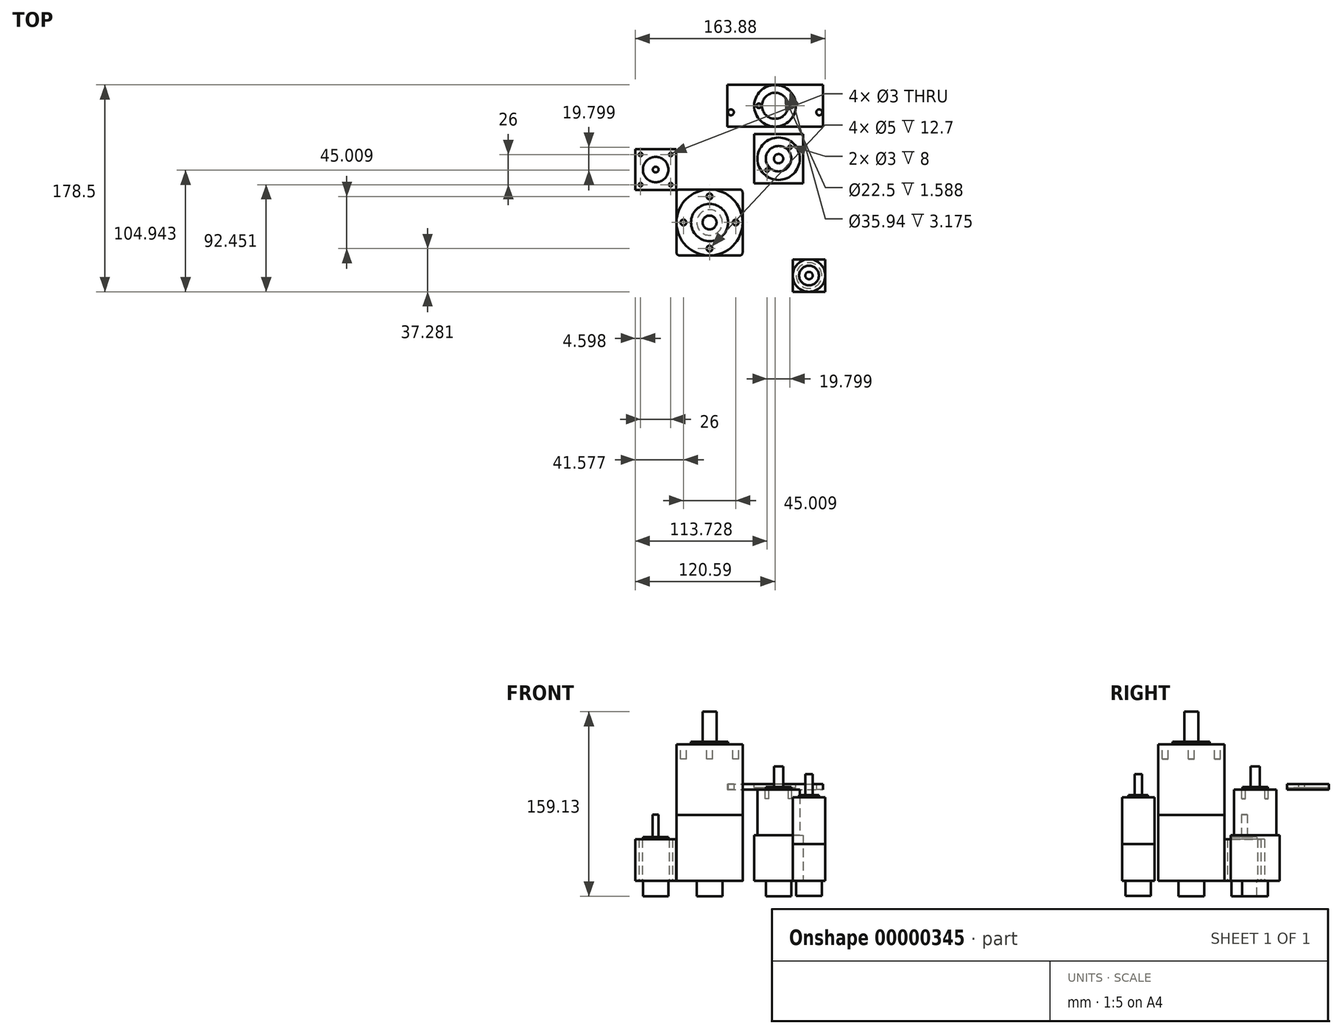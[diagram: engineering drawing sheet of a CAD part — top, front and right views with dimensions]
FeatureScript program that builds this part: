
annotation { "Feature Type Name" : "Feature", "Feature Type Description" : "" }
export const myFeature = defineFeature(function(context is Context, id is Id, definition is map)
    precondition{}
    {
        {
            var Q0;
            Q0=qCreatedBy(makeId("Top.planeOp"),FACE);
            var sketch = newSketch(context, id + "F0", { "sketchPlane" : qUnion([Q0])});
            skLineSegment(sketch, "E0.bottom", {"start": v(-20.35, 13.53) * mm, "end": v(31.57, 13.53) * mm});
            skLineSegment(sketch, "E0.top", {"start": v(-20.35, -43.46) * mm, "end": v(31.57, -43.46) * mm});
            skLineSegment(sketch, "E0.left", {"start": v(-22.89, 11) * mm, "end": v(-22.89, -40.92) * mm});
            skLineSegment(sketch, "E0.right", {"start": v(34.11, 11) * mm, "end": v(34.11, -40.92) * mm});
            skLineSegment(sketch, "E1", {"start": v(-22.89, 13.53) * mm, "end": v(34.11, -43.46) * mm, "construction": true});
            skLineSegment(sketch, "E2", {"start": v(34.11, 13.53) * mm, "end": v(-22.89, -43.46) * mm, "construction": true});
            skCircle(sketch, "E3", {"center": v(5.61, -14.96) * mm, "radius": 28.5 * mm, "construction": true});
            skPoint(sketch, "E4.visualSharp", {"position": v(-22.89, 13.53) * mm});
            skArc(sketch, "E4.filletArc", {"start": v(-20.35, 13.53) * mm, "mid": v(-22.14, 12.8) * mm, "end": v(-22.89, 11) * mm});
            skPoint(sketch, "E5.visualSharp", {"position": v(34.11, 13.53) * mm});
            skArc(sketch, "E5.filletArc", {"start": v(34.11, 11) * mm, "mid": v(33.37, 12.8) * mm, "end": v(31.57, 13.53) * mm});
            skPoint(sketch, "E6.visualSharp", {"position": v(34.11, -43.46) * mm});
            skArc(sketch, "E6.filletArc", {"start": v(31.57, -43.46) * mm, "mid": v(33.37, -42.72) * mm, "end": v(34.11, -40.92) * mm});
            skPoint(sketch, "E7.visualSharp", {"position": v(-22.89, -43.46) * mm});
            skArc(sketch, "E7.filletArc", {"start": v(-22.89, -40.92) * mm, "mid": v(-22.14, -42.72) * mm, "end": v(-20.35, -43.46) * mm});
            skSolve(sketch);
        }
        {
            var Q0;
            Q0=makeQuery(id+"F0.imprint","IMPRINT",FACE,{"disambiguationData":[TD([[makeQuery(id+"F0.imprint","IMPRINT",EDGE,{"derivedFrom":sQuery(id+"F0.wireOp",EDGE,"E0.bottom")}),-1.0]])]});
            extrude(context, id + "F1", {"entities" : qUnion([Q0]), "depth" : 57.02 * mm});
        }
        {
            var Q0;
            Q0=makeQuery(id+"F1.opExtrude","CAP_FACE",FACE,{"disambiguationData":[OSD([sQuery(id+"F0.wireOp",EDGE,"E0.bottom"),sQuery(id+"F0.wireOp",EDGE,"E0.top"),sQuery(id+"F0.wireOp",EDGE,"E0.left"),sQuery(id+"F0.wireOp",EDGE,"E0.right"),sQuery(id+"F0.wireOp",EDGE,"E4.filletArc"),sQuery(id+"F0.wireOp",EDGE,"E5.filletArc"),sQuery(id+"F0.wireOp",EDGE,"E6.filletArc"),sQuery(id+"F0.wireOp",EDGE,"E7.filletArc")])],"isStart":false});
            var sketch = newSketch(context, id + "F2", { "sketchPlane" : qUnion([Q0])});
            skCircle(sketch, "E8", {"center": v(5.61, -14.96) * mm, "radius": 28.5 * mm});
            skSolve(sketch);
        }
        {
            var Q0;
            {var subQ0=sQuery(id+"F2.wireOp",EDGE,"E8");var subQ4=makeQuery(id+"F2.imprint","INTERSECT",VERTEX,{"derivedFrom":[makeQuery(id+"F1.opExtrude","CAP_EDGE",EDGE,{"disambiguationData":[OSD([sQuery(id+"F0.wireOp",EDGE,"E0.bottom")])],"isStart":false}),subQ0]});Q0=makeQuery(id+"F2.imprint","IMPRINT",FACE,{"disambiguationData":[TD([[makeQuery(id+"F2.imprint","IMPRINT",EDGE,{"disambiguationData":[TD([[subQ4,1.0]])],"derivedFrom":subQ0}),1.0]])]});}
            extrude(context, id + "F3", {"entities" : qUnion([Q0]), "operationType" : NewBodyOperationType.ADD, "depth" : 61 * mm});
        }
        {
            var Q0;
            Q0=makeQuery(id+"F3.opExtrude","CAP_FACE",FACE,{"disambiguationData":[OSD([sQuery(id+"F2.wireOp",EDGE,"E8")])],"isStart":false});
            var sketch = newSketch(context, id + "F4", { "sketchPlane" : qUnion([Q0])});
            skCircle(sketch, "E9", {"center": v(5.61, -14.96) * mm, "radius": 16 * mm});
            skSolve(sketch);
        }
        {
            var Q0;
            Q0=makeQuery(id+"F4.imprint","IMPRINT",FACE,{"disambiguationData":[TD([[makeQuery(id+"F4.imprint","IMPRINT",EDGE,{"derivedFrom":sQuery(id+"F4.wireOp",EDGE,"E9")}),1.0]])]});
            extrude(context, id + "F5", {"entities" : qUnion([Q0]), "operationType" : NewBodyOperationType.ADD, "depth" : 2 * mm});
        }
        {
            var Q0;
            Q0=makeQuery(id+"F5.opExtrude","CAP_FACE",FACE,{"disambiguationData":[OSD([sQuery(id+"F4.wireOp",EDGE,"E9")])],"isStart":false});
            var sketch = newSketch(context, id + "F6", { "sketchPlane" : qUnion([Q0])});
            skCircle(sketch, "E10", {"center": v(5.61, -14.96) * mm, "radius": 6 * mm});
            skSolve(sketch);
        }
        {
            var Q0;
            Q0=makeQuery(id+"F6.imprint","IMPRINT",FACE,{"disambiguationData":[TD([[makeQuery(id+"F6.imprint","IMPRINT",EDGE,{"derivedFrom":sQuery(id+"F6.wireOp",EDGE,"E10")}),1.0]])]});
            extrude(context, id + "F7", {"entities" : qUnion([Q0]), "operationType" : NewBodyOperationType.ADD, "depth" : 26 * mm});
        }
        {
            var Q0;
            Q0=makeQuery(id+"F3.opExtrude","CAP_FACE",FACE,{"disambiguationData":[OSD([sQuery(id+"F2.wireOp",EDGE,"E8")])],"isStart":false});
            var sketch = newSketch(context, id + "F8", { "sketchPlane" : qUnion([Q0])});
            skCircle(sketch, "E11", {"center": v(5.61, -14.96) * mm, "radius": 22.5 * mm, "construction": true});
            skCircle(sketch, "E12", {"center": v(5.61, 7.54) * mm, "radius": 2.5 * mm});
            skCircle(sketch, "E13", {"center": v(28.12, -14.96) * mm, "radius": 2.5 * mm});
            skCircle(sketch, "E14", {"center": v(5.61, -37.47) * mm, "radius": 2.5 * mm});
            skCircle(sketch, "E15", {"center": v(-16.9, -14.96) * mm, "radius": 2.5 * mm});
            skSolve(sketch);
        }
        {
            var Q0;
            {Q0=qUnion([makeQuery(id+"F8.imprint","IMPRINT",FACE,{"disambiguationData":[TD([[makeQuery(id+"F8.imprint","IMPRINT",EDGE,{"derivedFrom":sQuery(id+"F8.wireOp",EDGE,"E12")}),1.0]])]}),makeQuery(id+"F8.imprint","IMPRINT",FACE,{"disambiguationData":[TD([[makeQuery(id+"F8.imprint","IMPRINT",EDGE,{"derivedFrom":sQuery(id+"F8.wireOp",EDGE,"E13")}),1.0]])]}),makeQuery(id+"F8.imprint","IMPRINT",FACE,{"disambiguationData":[TD([[makeQuery(id+"F8.imprint","IMPRINT",EDGE,{"derivedFrom":sQuery(id+"F8.wireOp",EDGE,"E14")}),1.0]])]}),makeQuery(id+"F8.imprint","IMPRINT",FACE,{"disambiguationData":[TD([[makeQuery(id+"F8.imprint","IMPRINT",EDGE,{"derivedFrom":sQuery(id+"F8.wireOp",EDGE,"E15")}),1.0]])]})]);}
            extrude(context, id + "F9", {"entities" : qUnion([Q0]), "operationType" : NewBodyOperationType.REMOVE, "oppositeDirection" : true, "depth" : 12.7 * mm});
        }
        {
            var Q0;
            Q0=qCreatedBy(makeId("Top.planeOp"),FACE);
            var sketch = newSketch(context, id + "F10", { "sketchPlane" : qUnion([Q0])});
            skLineSegment(sketch, "E16.bottom", {"start": v(44.01, 61.24) * mm, "end": v(86.3, 61.24) * mm});
            skLineSegment(sketch, "E16.top", {"start": v(44.01, 18.95) * mm, "end": v(86.3, 18.95) * mm});
            skLineSegment(sketch, "E16.left", {"start": v(44.01, 61.24) * mm, "end": v(44.01, 18.95) * mm});
            skLineSegment(sketch, "E16.right", {"start": v(86.3, 61.24) * mm, "end": v(86.3, 18.95) * mm});
            skSolve(sketch);
        }
        {
            var Q0;
            Q0=makeQuery(id+"F10.imprint","IMPRINT",FACE,{"disambiguationData":[TD([[makeQuery(id+"F10.imprint","IMPRINT",EDGE,{"derivedFrom":sQuery(id+"F10.wireOp",EDGE,"E16.bottom")}),-1.0]])]});
            extrude(context, id + "F11", {"entities" : qUnion([Q0]), "depth" : 39.5 * mm});
        }
        {
            var Q0;
            Q0=makeQuery(id+"F11.opExtrude","CAP_FACE",FACE,{"disambiguationData":[OSD([sQuery(id+"F10.wireOp",EDGE,"E16.bottom"),sQuery(id+"F10.wireOp",EDGE,"E16.top"),sQuery(id+"F10.wireOp",EDGE,"E16.left"),sQuery(id+"F10.wireOp",EDGE,"E16.right")])],"isStart":false});
            var sketch = newSketch(context, id + "F12", { "sketchPlane" : qUnion([Q0])});
            skCircle(sketch, "E17", {"center": v(65.16, 40.1) * mm, "radius": 21.15 * mm, "construction": true});
            skCircle(sketch, "E18", {"center": v(65.16, 40.1) * mm, "radius": 18.29 * mm});
            skSolve(sketch);
        }
        {
            var Q0;
            Q0=makeQuery(id+"F12.imprint","IMPRINT",FACE,{"disambiguationData":[TD([[makeQuery(id+"F12.imprint","IMPRINT",EDGE,{"derivedFrom":sQuery(id+"F12.wireOp",EDGE,"E18")}),1.0]])]});
            extrude(context, id + "F13", {"entities" : qUnion([Q0]), "operationType" : NewBodyOperationType.ADD, "depth" : 39.5 * mm});
        }
        {
            var Q0;
            Q0=makeQuery(id+"F13.opExtrude","CAP_FACE",FACE,{"disambiguationData":[OSD([sQuery(id+"F12.wireOp",EDGE,"E18")])],"isStart":false});
            var sketch = newSketch(context, id + "F14", { "sketchPlane" : qUnion([Q0])});
            skCircle(sketch, "E19", {"center": v(65.16, 40.1) * mm, "radius": 11 * mm});
            skSolve(sketch);
        }
        {
            var Q0;
            Q0=makeQuery(id+"F14.imprint","IMPRINT",FACE,{"disambiguationData":[TD([[makeQuery(id+"F14.imprint","IMPRINT",EDGE,{"derivedFrom":sQuery(id+"F14.wireOp",EDGE,"E19")}),1.0]])]});
            extrude(context, id + "F15", {"entities" : qUnion([Q0]), "operationType" : NewBodyOperationType.ADD, "depth" : 1.98 * mm});
        }
        {
            var Q0;
            Q0=makeQuery(id+"F15.opExtrude","CAP_FACE",FACE,{"disambiguationData":[OSD([sQuery(id+"F14.wireOp",EDGE,"E19")])],"isStart":false});
            var sketch = newSketch(context, id + "F16", { "sketchPlane" : qUnion([Q0])});
            skCircle(sketch, "E20", {"center": v(65.16, 40.1) * mm, "radius": 4 * mm});
            skSolve(sketch);
        }
        {
            var Q0;
            Q0=makeQuery(id+"F16.imprint","IMPRINT",FACE,{"disambiguationData":[TD([[makeQuery(id+"F16.imprint","IMPRINT",EDGE,{"derivedFrom":sQuery(id+"F16.wireOp",EDGE,"E20")}),1.0]])]});
            extrude(context, id + "F17", {"entities" : qUnion([Q0]), "operationType" : NewBodyOperationType.ADD, "depth" : 18 * mm});
        }
        {
            var Q0;
            Q0=qCreatedBy(makeId("Top.planeOp"),FACE);
            var sketch = newSketch(context, id + "F18", { "sketchPlane" : qUnion([Q0])});
            skLineSegment(sketch, "E21.bottom", {"start": v(77.42, -46.76) * mm, "end": v(105.4, -46.76) * mm});
            skLineSegment(sketch, "E21.top", {"start": v(77.42, -74.75) * mm, "end": v(105.4, -74.75) * mm});
            skLineSegment(sketch, "E21.left", {"start": v(77.42, -46.76) * mm, "end": v(77.42, -74.75) * mm});
            skLineSegment(sketch, "E21.right", {"start": v(105.4, -46.76) * mm, "end": v(105.4, -74.75) * mm});
            skSolve(sketch);
        }
        {
            var Q0;
            Q0=makeQuery(id+"F18.imprint","IMPRINT",FACE,{"disambiguationData":[TD([[makeQuery(id+"F18.imprint","IMPRINT",EDGE,{"derivedFrom":sQuery(id+"F18.wireOp",EDGE,"E21.bottom")}),-1.0]])]});
            extrude(context, id + "F19", {"entities" : qUnion([Q0]), "depth" : 32 * mm});
        }
        {
            var Q0;
            Q0=makeQuery(id+"F19.opExtrude","CAP_FACE",FACE,{"disambiguationData":[OSD([sQuery(id+"F18.wireOp",EDGE,"E21.bottom"),sQuery(id+"F18.wireOp",EDGE,"E21.top"),sQuery(id+"F18.wireOp",EDGE,"E21.left"),sQuery(id+"F18.wireOp",EDGE,"E21.right")])],"isStart":false});
            var sketch = newSketch(context, id + "F20", { "sketchPlane" : qUnion([Q0])});
            skLineSegment(sketch, "E22.0.0", {"start": v(77.42, -46.76) * mm, "end": v(105.4, -46.76) * mm, "construction": true});
            skLineSegment(sketch, "E22.0.1", {"start": v(77.42, -46.76) * mm, "end": v(77.42, -74.75) * mm, "construction": true});
            skLineSegment(sketch, "E22.0.2", {"start": v(77.42, -74.75) * mm, "end": v(105.4, -74.75) * mm, "construction": true});
            skLineSegment(sketch, "E22.0.3", {"start": v(105.4, -46.76) * mm, "end": v(105.4, -74.75) * mm, "construction": true});
            skLineSegment(sketch, "E23", {"start": v(77.42, -46.76) * mm, "end": v(105.4, -74.75) * mm, "construction": true});
            skCircle(sketch, "E24", {"center": v(91.41, -60.75) * mm, "radius": 14 * mm});
            skSolve(sketch);
        }
        {
            var Q0;
            {var subQ0=sQuery(id+"F20.wireOp",EDGE,"E24");var subQ4=makeQuery(id+"F20.imprint","INTERSECT",VERTEX,{"derivedFrom":[makeQuery(id+"F19.opExtrude","CAP_EDGE",EDGE,{"disambiguationData":[OSD([sQuery(id+"F18.wireOp",EDGE,"E21.bottom")])],"isStart":false}),subQ0]});Q0=makeQuery(id+"F20.imprint","IMPRINT",FACE,{"disambiguationData":[TD([[makeQuery(id+"F20.imprint","IMPRINT",EDGE,{"disambiguationData":[TD([[subQ4,1.0]])],"derivedFrom":subQ0}),1.0]])]});}
            extrude(context, id + "F21", {"entities" : qUnion([Q0]), "operationType" : NewBodyOperationType.ADD, "depth" : 40.1 * mm});
        }
        {
            var Q0;
            Q0=makeQuery(id+"F21.opExtrude","CAP_FACE",FACE,{"disambiguationData":[OSD([sQuery(id+"F20.wireOp",EDGE,"E24")])],"isStart":false});
            var sketch = newSketch(context, id + "F22", { "sketchPlane" : qUnion([Q0])});
            skCircle(sketch, "E25", {"center": v(91.41, -60.75) * mm, "radius": 8.5 * mm});
            skSolve(sketch);
        }
        {
            var Q0;
            Q0=makeQuery(id+"F22.imprint","IMPRINT",FACE,{"disambiguationData":[TD([[makeQuery(id+"F22.imprint","IMPRINT",EDGE,{"derivedFrom":sQuery(id+"F22.wireOp",EDGE,"E25")}),1.0]])]});
            extrude(context, id + "F23", {"entities" : qUnion([Q0]), "operationType" : NewBodyOperationType.ADD, "depth" : 1.98 * mm});
        }
        {
            var Q0;
            Q0=makeQuery(id+"F23.opExtrude","CAP_FACE",FACE,{"disambiguationData":[OSD([sQuery(id+"F22.wireOp",EDGE,"E25")])],"isStart":false});
            var sketch = newSketch(context, id + "F24", { "sketchPlane" : qUnion([Q0])});
            skCircle(sketch, "E26", {"center": v(91.41, -60.75) * mm, "radius": 3.18 * mm});
            skSolve(sketch);
        }
        {
            var Q0;
            Q0=makeQuery(id+"F24.imprint","IMPRINT",FACE,{"disambiguationData":[TD([[makeQuery(id+"F24.imprint","IMPRINT",EDGE,{"derivedFrom":sQuery(id+"F24.wireOp",EDGE,"E26")}),1.0]])]});
            extrude(context, id + "F25", {"entities" : qUnion([Q0]), "operationType" : NewBodyOperationType.ADD, "depth" : 18.03 * mm});
        }
        {
            var Q0;
            Q0=qCreatedBy(makeId("Top.planeOp"),FACE);
            var sketch = newSketch(context, id + "F26", { "sketchPlane" : qUnion([Q0])});
            skLineSegment(sketch, "E27.bottom", {"start": v(-58.47, 48.3) * mm, "end": v(-23.27, 48.3) * mm});
            skLineSegment(sketch, "E27.top", {"start": v(-58.47, 13.1) * mm, "end": v(-23.27, 13.1) * mm});
            skLineSegment(sketch, "E27.left", {"start": v(-58.47, 48.3) * mm, "end": v(-58.47, 13.1) * mm});
            skLineSegment(sketch, "E27.right", {"start": v(-23.27, 48.3) * mm, "end": v(-23.27, 13.1) * mm});
            skLineSegment(sketch, "E28.bottom", {"start": v(-53.87, 43.7) * mm, "end": v(-27.87, 43.7) * mm, "construction": true});
            skLineSegment(sketch, "E28.top", {"start": v(-53.87, 17.7) * mm, "end": v(-27.87, 17.7) * mm, "construction": true});
            skLineSegment(sketch, "E28.left", {"start": v(-53.87, 43.7) * mm, "end": v(-53.87, 17.7) * mm, "construction": true});
            skLineSegment(sketch, "E28.right", {"start": v(-27.87, 43.7) * mm, "end": v(-27.87, 17.7) * mm, "construction": true});
            skLineSegment(sketch, "E29", {"start": v(-40.87, 48.3) * mm, "end": v(-40.87, 13.1) * mm, "construction": true});
            skLineSegment(sketch, "E30", {"start": v(-58.47, 30.7) * mm, "end": v(-23.27, 30.7) * mm, "construction": true});
            skCircle(sketch, "E31", {"center": v(-53.87, 43.7) * mm, "radius": 1.5 * mm});
            skCircle(sketch, "E32", {"center": v(-27.87, 43.7) * mm, "radius": 1.5 * mm});
            skCircle(sketch, "E33", {"center": v(-27.87, 17.7) * mm, "radius": 1.5 * mm});
            skCircle(sketch, "E34", {"center": v(-53.87, 17.7) * mm, "radius": 1.5 * mm});
            skSolve(sketch);
        }
        {
            var Q0;
            Q0=makeQuery(id+"F26.imprint","IMPRINT",FACE,{"disambiguationData":[TD([[makeQuery(id+"F26.imprint","IMPRINT",EDGE,{"derivedFrom":sQuery(id+"F26.wireOp",EDGE,"E27.bottom")}),-1.0]])]});
            extrude(context, id + "F27", {"entities" : qUnion([Q0]), "depth" : 36.07 * mm});
        }
        {
            var Q0;
            Q0=makeQuery(id+"F27.opExtrude","CAP_FACE",FACE,{"disambiguationData":[OSD([sQuery(id+"F26.wireOp",EDGE,"E27.bottom"),sQuery(id+"F26.wireOp",EDGE,"E27.top"),sQuery(id+"F26.wireOp",EDGE,"E27.left"),sQuery(id+"F26.wireOp",EDGE,"E27.right")])],"isStart":false});
            var sketch = newSketch(context, id + "F28", { "sketchPlane" : qUnion([Q0])});
            skCircle(sketch, "E35", {"center": v(-40.87, 30.7) * mm, "radius": 11 * mm});
            skLineSegment(sketch, "E36", {"start": v(-58.47, 13.1) * mm, "end": v(-23.27, 48.3) * mm, "construction": true});
            skSolve(sketch);
        }
        {
            var Q0;
            Q0=makeQuery(id+"F28.imprint","IMPRINT",FACE,{"disambiguationData":[TD([[makeQuery(id+"F28.imprint","IMPRINT",EDGE,{"derivedFrom":sQuery(id+"F28.wireOp",EDGE,"E35")}),1.0]])]});
            extrude(context, id + "F29", {"entities" : qUnion([Q0]), "operationType" : NewBodyOperationType.ADD, "depth" : 1.98 * mm});
        }
        {
            var Q0;
            Q0=makeQuery(id+"F29.opExtrude","CAP_FACE",FACE,{"disambiguationData":[OSD([sQuery(id+"F28.wireOp",EDGE,"E35")])],"isStart":false});
            var sketch = newSketch(context, id + "F30", { "sketchPlane" : qUnion([Q0])});
            skCircle(sketch, "E37", {"center": v(-40.87, 30.7) * mm, "radius": 2.5 * mm});
            skSolve(sketch);
        }
        {
            var Q0;
            Q0=makeQuery(id+"F30.imprint","IMPRINT",FACE,{"disambiguationData":[TD([[makeQuery(id+"F30.imprint","IMPRINT",EDGE,{"derivedFrom":sQuery(id+"F30.wireOp",EDGE,"E37")}),1.0]])]});
            extrude(context, id + "F31", {"entities" : qUnion([Q0]), "operationType" : NewBodyOperationType.ADD, "depth" : 19.3 * mm});
        }
        {
            var Q0;
            Q0=makeQuery(id+"F19.opExtrude","CAP_FACE",FACE,{"disambiguationData":[OSD([sQuery(id+"F18.wireOp",EDGE,"E21.bottom"),sQuery(id+"F18.wireOp",EDGE,"E21.top"),sQuery(id+"F18.wireOp",EDGE,"E21.left"),sQuery(id+"F18.wireOp",EDGE,"E21.right")])],"isStart":true});
            var sketch = newSketch(context, id + "F32", { "sketchPlane" : qUnion([Q0])});
            skCircle(sketch, "E38", {"center": v(91.41, 60.75) * mm, "radius": 11.05 * mm});
            skPoint(sketch, "E38.centerSnap0", {"position": v(105.4, 60.75) * mm});
            skPoint(sketch, "E38.centerSnap1", {"position": v(91.41, 74.75) * mm});
            skSolve(sketch);
        }
        {
            var Q0;
            Q0 = qSketchRegion(id + "F32", true);
            extrude(context, id + "F33", {"entities" : qUnion([Q0]), "operationType" : NewBodyOperationType.ADD, "depth" : 13 * mm});
        }
        {
            var Q0;
            Q0=makeQuery(id+"F11.opExtrude","CAP_FACE",FACE,{"disambiguationData":[OSD([sQuery(id+"F10.wireOp",EDGE,"E16.bottom"),sQuery(id+"F10.wireOp",EDGE,"E16.top"),sQuery(id+"F10.wireOp",EDGE,"E16.left"),sQuery(id+"F10.wireOp",EDGE,"E16.right")])],"isStart":true});
            var sketch = newSketch(context, id + "F34", { "sketchPlane" : qUnion([Q0])});
            skCircle(sketch, "E39", {"center": v(65.16, -40.1) * mm, "radius": 11.05 * mm});
            skPoint(sketch, "E39.centerSnap0", {"position": v(86.3, -40.1) * mm});
            skPoint(sketch, "E39.centerSnap1", {"position": v(65.16, -18.95) * mm});
            skSolve(sketch);
        }
        {
            var Q0;
            Q0 = qSketchRegion(id + "F34", true);
            extrude(context, id + "F35", {"entities" : qUnion([Q0]), "operationType" : NewBodyOperationType.ADD, "depth" : 13.08 * mm});
        }
        {
            var Q0;
            Q0=makeQuery(id+"F1.opExtrude","CAP_FACE",FACE,{"disambiguationData":[OSD([sQuery(id+"F0.wireOp",EDGE,"E0.bottom"),sQuery(id+"F0.wireOp",EDGE,"E0.top"),sQuery(id+"F0.wireOp",EDGE,"E0.left"),sQuery(id+"F0.wireOp",EDGE,"E0.right"),sQuery(id+"F0.wireOp",EDGE,"E4.filletArc"),sQuery(id+"F0.wireOp",EDGE,"E5.filletArc"),sQuery(id+"F0.wireOp",EDGE,"E6.filletArc"),sQuery(id+"F0.wireOp",EDGE,"E7.filletArc")])],"isStart":true});
            var sketch = newSketch(context, id + "F36", { "sketchPlane" : qUnion([Q0])});
            skCircle(sketch, "E40", {"center": v(5.61, 14.96) * mm, "radius": 11.05 * mm});
            skPoint(sketch, "E40.centerSnap0", {"position": v(34.11, 14.96) * mm});
            skPoint(sketch, "E40.centerSnap1", {"position": v(5.61, 43.46) * mm});
            skSolve(sketch);
        }
        {
            var Q0;
            Q0 = qSketchRegion(id + "F36", true);
            extrude(context, id + "F37", {"entities" : qUnion([Q0]), "operationType" : NewBodyOperationType.ADD, "depth" : 13.08 * mm});
        }
        {
            var Q0;
            Q0=makeQuery(id+"F27.opExtrude","CAP_FACE",FACE,{"disambiguationData":[OSD([sQuery(id+"F26.wireOp",EDGE,"E27.bottom"),sQuery(id+"F26.wireOp",EDGE,"E27.top"),sQuery(id+"F26.wireOp",EDGE,"E27.left"),sQuery(id+"F26.wireOp",EDGE,"E27.right"),sQuery(id+"F26.wireOp",EDGE,"E31"),sQuery(id+"F26.wireOp",EDGE,"E32"),sQuery(id+"F26.wireOp",EDGE,"E33"),sQuery(id+"F26.wireOp",EDGE,"E34")])],"isStart":true});
            var sketch = newSketch(context, id + "F38", { "sketchPlane" : qUnion([Q0])});
            skCircle(sketch, "E41", {"center": v(-40.87, -30.7) * mm, "radius": 11.05 * mm});
            skPoint(sketch, "E41.centerSnap0", {"position": v(-23.27, -30.7) * mm});
            skPoint(sketch, "E41.centerSnap1", {"position": v(-40.87, -13.1) * mm});
            skSolve(sketch);
        }
        {
            var Q0;
            Q0 = qSketchRegion(id + "F38", true);
            extrude(context, id + "F39", {"entities" : qUnion([Q0]), "operationType" : NewBodyOperationType.ADD, "depth" : 13.08 * mm});
        }
        {
            var Q0;
            Q0=makeQuery(id+"F13.opExtrude","CAP_FACE",FACE,{"disambiguationData":[OSD([sQuery(id+"F12.wireOp",EDGE,"E18")])],"isStart":false});
            var sketch = newSketch(context, id + "F40", { "sketchPlane" : qUnion([Q0])});
            skCircle(sketch, "E42", {"center": v(65.16, 40.1) * mm, "radius": 14 * mm, "construction": true});
            skCircle(sketch, "E43", {"center": v(75.06, 50) * mm, "radius": 1.5 * mm});
            skCircle(sketch, "E44", {"center": v(55.26, 30.2) * mm, "radius": 1.5 * mm});
            skLineSegment(sketch, "E45.0.0", {"start": v(86.3, 61.24) * mm, "end": v(44.01, 61.24) * mm, "construction": true});
            skLineSegment(sketch, "E45.0.1", {"start": v(44.01, 61.24) * mm, "end": v(44.01, 18.95) * mm, "construction": true});
            skLineSegment(sketch, "E45.0.2", {"start": v(44.01, 18.95) * mm, "end": v(86.3, 18.95) * mm, "construction": true});
            skLineSegment(sketch, "E45.0.3", {"start": v(86.3, 18.95) * mm, "end": v(86.3, 61.24) * mm, "construction": true});
            skLineSegment(sketch, "E46", {"start": v(86.3, 61.24) * mm, "end": v(44.01, 18.95) * mm, "construction": true});
            skSolve(sketch);
        }
        {
            var Q0;
            Q0 = qSketchRegion(id + "F40", true);
            extrude(context, id + "F41", {"entities" : qUnion([Q0]), "operationType" : NewBodyOperationType.REMOVE, "oppositeDirection" : true, "depth" : 8 * mm});
        }
        {
            var Q0;
            Q0=makeQuery(id+"F13.opExtrude","CAP_FACE",FACE,{"disambiguationData":[OSD([sQuery(id+"F12.wireOp",EDGE,"E18")])],"isStart":false});
            var sketch = newSketch(context, id + "F42", { "sketchPlane" : qUnion([Q0])});
            skLineSegment(sketch, "E47.bottom", {"start": v(20.85, 103.75) * mm, "end": v(103.4, 103.75) * mm});
            skLineSegment(sketch, "E47.top", {"start": v(20.85, 67.75) * mm, "end": v(103.4, 67.75) * mm});
            skLineSegment(sketch, "E47.left", {"start": v(20.85, 103.75) * mm, "end": v(20.85, 67.75) * mm});
            skLineSegment(sketch, "E47.right", {"start": v(103.4, 103.75) * mm, "end": v(103.4, 67.75) * mm});
            skCircle(sketch, "E48", {"center": v(62.12, 85.75) * mm, "radius": 11.25 * mm});
            skLineSegment(sketch, "E49", {"start": v(20.85, 85.75) * mm, "end": v(103.4, 85.75) * mm, "construction": true});
            skLineSegment(sketch, "E50", {"start": v(62.12, 103.75) * mm, "end": v(62.12, 67.75) * mm, "construction": true});
            skCircle(sketch, "E51", {"center": v(62.12, 85.75) * mm, "radius": 14 * mm, "construction": true});
            skCircle(sketch, "E52", {"center": v(48.12, 85.75) * mm, "radius": 2 * mm});
            skCircle(sketch, "E53", {"center": v(76.12, 85.75) * mm, "radius": 2 * mm});
            skCircle(sketch, "E54", {"center": v(100.22, 80.13) * mm, "radius": 2.55 * mm});
            skCircle(sketch, "E55", {"center": v(24.02, 80.13) * mm, "radius": 2.55 * mm});
            skSolve(sketch);
        }
        {
            var Q0;
            Q0 = qSketchRegion(id + "F42", true);
            extrude(context, id + "F43", {"entities" : qUnion([Q0]), "depth" : 4.76 * mm});
        }
        {
            var Q0;
            Q0=makeQuery(id+"F43.opExtrude","CAP_FACE",FACE,{"disambiguationData":[OSD([sQuery(id+"F42.wireOp",EDGE,"E47.bottom"),sQuery(id+"F42.wireOp",EDGE,"E47.top"),sQuery(id+"F42.wireOp",EDGE,"E47.left"),sQuery(id+"F42.wireOp",EDGE,"E47.right"),sQuery(id+"F42.wireOp",EDGE,"E48"),sQuery(id+"F42.wireOp",EDGE,"E52"),sQuery(id+"F42.wireOp",EDGE,"E53"),sQuery(id+"F42.wireOp",EDGE,"E54"),sQuery(id+"F42.wireOp",EDGE,"E55")])],"isStart":false});
            var sketch = newSketch(context, id + "F44", { "sketchPlane" : qUnion([Q0])});
            skCircle(sketch, "E56", {"center": v(62.12, 85.75) * mm, "radius": 17.97 * mm});
            skSolve(sketch);
        }
        {
            var Q0;
            Q0 = qSketchRegion(id + "F44", true);
            extrude(context, id + "F45", {"entities" : qUnion([Q0]), "operationType" : NewBodyOperationType.REMOVE, "oppositeDirection" : true, "depth" : 3.17 * mm});
        }
    });
